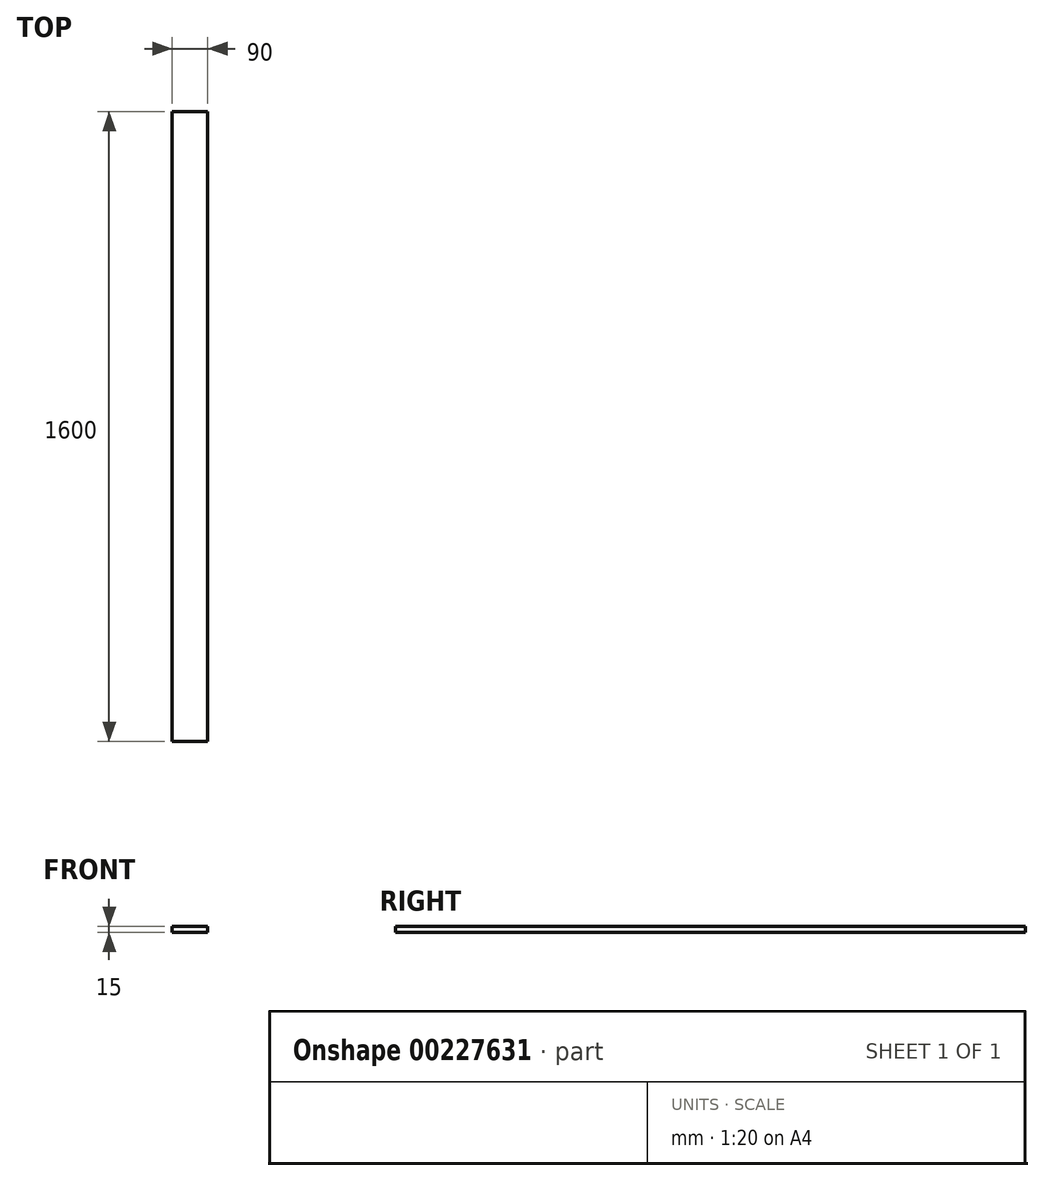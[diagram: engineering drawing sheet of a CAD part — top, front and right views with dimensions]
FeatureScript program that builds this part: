
annotation { "Feature Type Name" : "Feature", "Feature Type Description" : "" }
export const myFeature = defineFeature(function(context is Context, id is Id, definition is map)
    precondition{}
    {
        {
            var Q0;
            Q0=qCreatedBy(makeId("Front.planeOp"),FACE);
            var sketch = newSketch(context, id + "F0", { "sketchPlane" : qUnion([Q0])});
            skLineSegment(sketch, "E0.bottom", {"start": v(-41.96, 1.38) * mm, "end": v(48.04, 1.38) * mm});
            skLineSegment(sketch, "E0.top", {"start": v(-41.96, -13.62) * mm, "end": v(48.04, -13.62) * mm});
            skLineSegment(sketch, "E0.left", {"start": v(-41.96, 1.38) * mm, "end": v(-41.96, -13.62) * mm});
            skLineSegment(sketch, "E0.right", {"start": v(48.04, 1.38) * mm, "end": v(48.04, -13.62) * mm});
            skSolve(sketch);
        }
        {
            var Q0;
            Q0=makeQuery(id+"F0.imprint","IMPRINT",FACE,{"disambiguationData":[TD([[makeQuery(id+"F0.imprint","IMPRINT",EDGE,{"derivedFrom":sQuery(id+"F0.wireOp",EDGE,"E0.bottom")}),-1.0]])]});
            extrude(context, id + "F1", {"entities" : qUnion([Q0]), "oppositeDirection" : true, "depth" : 1600 * mm});
        }
    });
